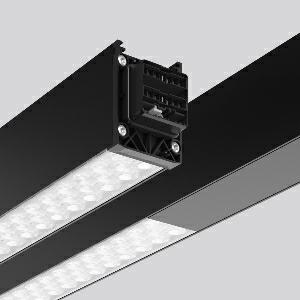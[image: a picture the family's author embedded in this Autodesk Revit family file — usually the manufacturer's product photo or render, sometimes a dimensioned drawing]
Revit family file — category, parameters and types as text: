
# Revit family: linedo_2_3m_90_1000_952390_853_400_704_a16c
name_source: partatom
category: Lighting Fixtures
units: mm (PartAtom-declared; Revit-internal decimal feet)

## family parameters
Cut with Voids When Loaded = No
Host = Face
Light Source = No
Part Type = Normal
Room Calculation Point = No
Round Connector Dimension = Use Diameter
Shared = No

## types (1)
- LINEDO_2,3m_90_1000 (1 x LED Modul 850, 5200 lm, 5000)
    Apparent Load = 38 VA
    CIE Flux Codes = 73 96 99 100 100
    Color Rendering = 80
    Color Temperature = 5000
    Default Elevation = 1800 mm
    Description = LINEDO, 38 W, 5200 lm, 850, black, on/off
Continuous line luminaire, L 2291 B 58 H 76
    Height = 76 mm
    Lamp = 1 x LED Modul 850
    Lamp Light Flux = 5200 lm
    Lamp count = 1
    Length = 2291 mm
    Lifetime = 50000 h
    Luminous efficacy = 137 lm/W
    Manufacturer = RZB
    ModVariant = No
    Model = 952390.853.400.704
    Mounting Place = Ceiling
    Mounting Type = Surface mounted, Pendant
    Number of Poles = 1
    OnlyDefault = Yes
    Power Factor = 1
    Product Name = LINEDO_2,3m_90_1000
    Product group = Surface mounted continuous line luminaire system
    ProductGroupID = 310
    Protection Class = Protection class I
    Protection Degree = IP 54
    RLX_Detail_Level = 1
    RLX_Emergency_Light_Flux = 0 lm
    RLX_Emergency_Type = 0
    RLX_Emergency_Type_DB = No
    RlxData = <blob elided: 56529 chars, md5=e007b754>
    Socket = socket
    Standby Power = 0 W
    System Light Flux = 5200 lm
    System Power = 38 W
    Type Comments = Product without accessories
    Type Image = 954590.853.476.504.jpg
    URL = http://relux.com
    VarID = ---
    Voltage = 230 V
    Voltage Range = 220-240 V
    Weight = 0.00 kg
    Width = 58 mm

## geometry (parser evidence)
native form markers: Blend x4, Sweep x14
no freeform markers — native parametric forms only
